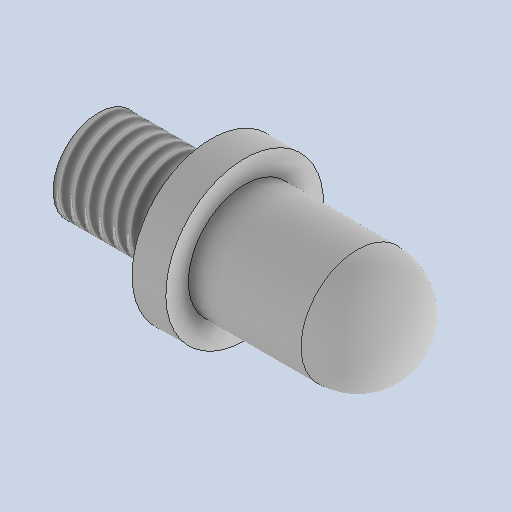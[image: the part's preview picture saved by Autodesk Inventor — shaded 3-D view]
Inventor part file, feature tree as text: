
AUTODESK INVENTOR PART (.ipt)
format: ipt  version: 2025.1 (Build 291241000, 241)  size: 152,576 bytes
history: native  units: mm
features: other x3, sketch x2
ambient origin geometry x8: Origin, YZ Plane, XZ Plane, XY Plane, X Axis, Y Axis, Z Axis, Center Point
bodies: Volumenkörper1 (feature_tree)
feature tree (5):
  other  "1156.ipt"
  other  "Volumenkörper1::1156.ipt"
  other  "TaggingFeature1"
  sketch  "Skizze1"  dims[d0=10.0mm]
  sketch  "Skizze2"
